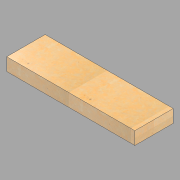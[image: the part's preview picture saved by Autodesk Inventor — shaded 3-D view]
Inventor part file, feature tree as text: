
AUTODESK INVENTOR PART (.ipt)
format: ipt  version: 2022.1 (Build 261234020, 234B)  size: 105,472 bytes
history: native  units: in
note: dims shown in document units (in); Inventor stores cm internally (conversion verified against a paired STEP export)
features: extrude x1, sketch x1
ambient origin geometry x8: Origin, YZ Plane, XZ Plane, XY Plane, X Axis, Y Axis, Z Axis, Center Point
bodies: Solid1 (feature_tree)
feature tree (2):
  extrude  "Extrusion1"  Depth=18.0in
  sketch  "Sketch1"  dims[d0=6.0in d1=18.0in d2=60.0in d3=0.0in]
